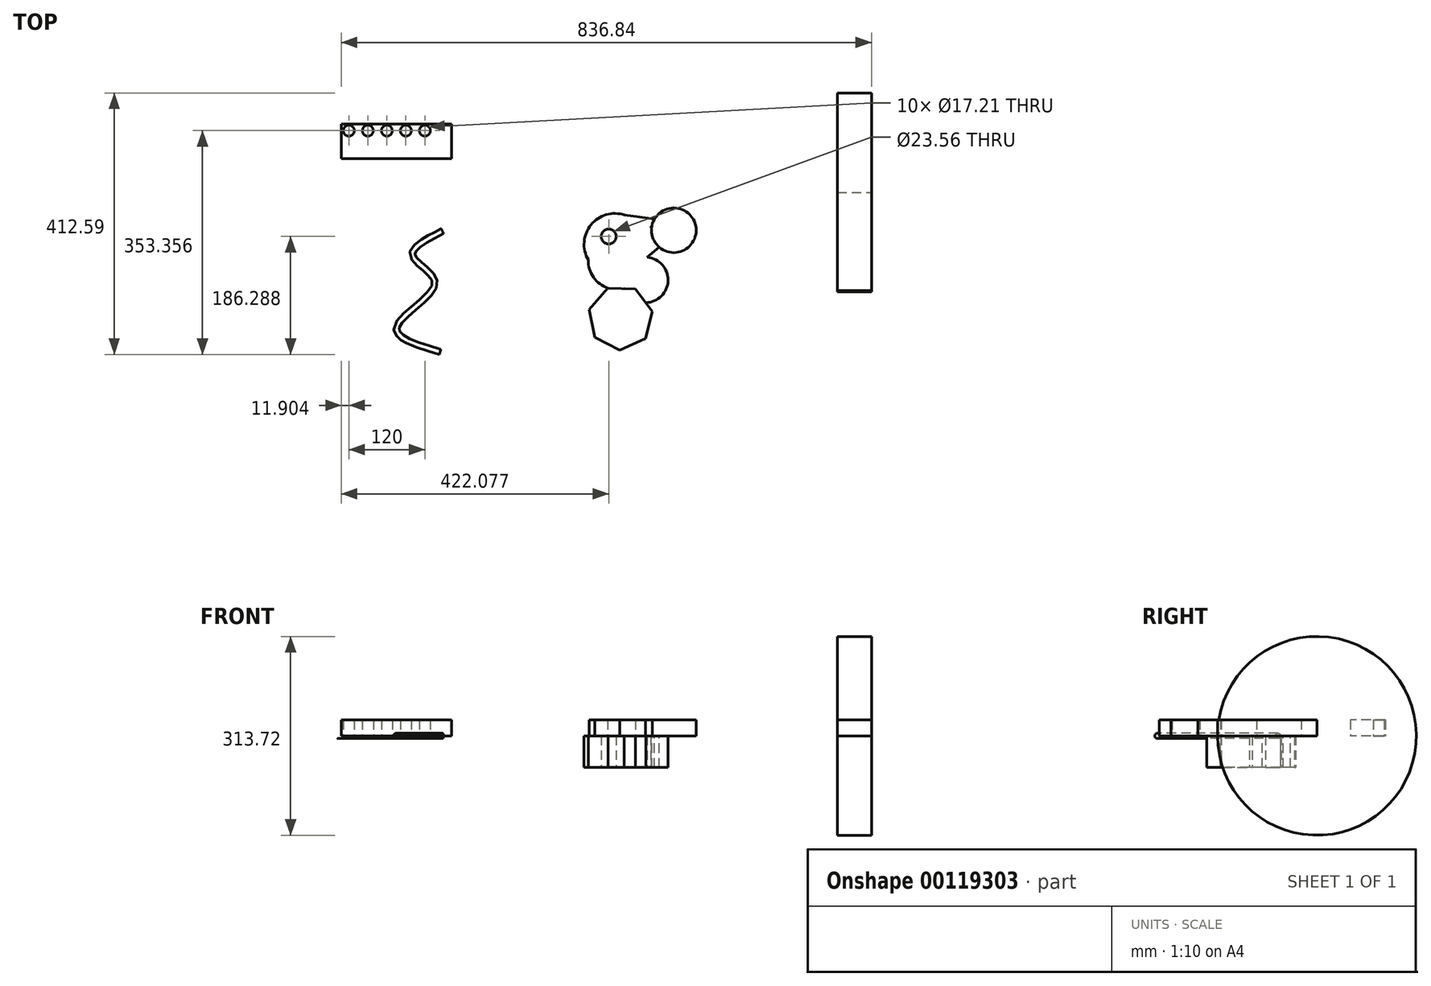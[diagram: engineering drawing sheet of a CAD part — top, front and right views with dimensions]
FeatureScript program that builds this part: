
annotation { "Feature Type Name" : "Feature", "Feature Type Description" : "" }
export const myFeature = defineFeature(function(context is Context, id is Id, definition is map)
    precondition{}
    {
        {
            var Q0;
            Q0=qCreatedBy(makeId("Top.planeOp"),FACE);
            var sketch = newSketch(context, id + "F0", { "sketchPlane" : qUnion([Q0])});
            skLineSegment(sketch, "E0", {"start": v(-37.14, 55.26) * mm, "end": v(11.62, 48.64) * mm});
            skLineSegment(sketch, "E1", {"start": v(11.62, 48.64) * mm, "end": v(4.36, 34.7) * mm});
            skLineSegment(sketch, "E2", {"start": v(4.36, 34.7) * mm, "end": v(23.23, 23.38) * mm});
            skLineSegment(sketch, "E3", {"start": v(23.23, 23.38) * mm, "end": v(40.66, 23.38) * mm});
            skLineSegment(sketch, "E4", {"start": v(40.66, 23.38) * mm, "end": v(-1.5, -11.44) * mm});
            skArc(sketch, "E5", {"start": v(-37.55, -60.76) * mm, "mid": v(24.6, -68.36) * mm, "end": v(-1.5, -11.44) * mm});
            skArc(sketch, "E6", {"start": v(-37.14, 55.26) * mm, "mid": v(-90.15, 39.64) * mm, "end": v(-94.6, -15.44) * mm});
            skArc(sketch, "E7", {"start": v(-94.6, -15.44) * mm, "mid": v(-77.4, -52.36) * mm, "end": v(-37.55, -60.76) * mm});
            skCircle(sketch, "E8", {"center": v(-62.13, 21.43) * mm, "radius": 11.78 * mm});
            skSolve(sketch);
        }
        {
            var Q0;
            Q0=makeQuery(id+"F0.imprint","IMPRINT",FACE,{"disambiguationData":[TD([[makeQuery(id+"F0.imprint","IMPRINT",EDGE,{"derivedFrom":sQuery(id+"F0.wireOp",EDGE,"E0")}),-1.0]])]});
            extrude(context, id + "F1", {"entities" : qUnion([Q0]), "depth" : 50 * mm});
        }
        {
            var Q0;
            Q0=makeQuery(id+"F1.opExtrude","CAP_FACE",FACE,{"disambiguationData":[OSD([sQuery(id+"F0.wireOp",EDGE,"E0"),sQuery(id+"F0.wireOp",EDGE,"E1"),sQuery(id+"F0.wireOp",EDGE,"E2"),sQuery(id+"F0.wireOp",EDGE,"E3"),sQuery(id+"F0.wireOp",EDGE,"E4"),sQuery(id+"F0.wireOp",EDGE,"E5"),sQuery(id+"F0.wireOp",EDGE,"E6"),sQuery(id+"F0.wireOp",EDGE,"E7")])],"isStart":false});
            var sketch = newSketch(context, id + "F2", { "sketchPlane" : qUnion([Q0])});
            skCircle(sketch, "E9.cCircle", {"center": v(-43.3, -106.73) * mm, "radius": 46.05 * mm, "construction": true});
            skLineSegment(sketch, "E9.0", {"start": v(-19.76, -61.36) * mm, "end": v(6.86, -96.85) * mm});
            skLineSegment(sketch, "E9.1", {"start": v(6.86, -96.85) * mm, "end": v(-4.3, -139.78) * mm});
            skLineSegment(sketch, "E9.2", {"start": v(-4.3, -139.78) * mm, "end": v(-44.8, -157.83) * mm});
            skLineSegment(sketch, "E9.3", {"start": v(-44.8, -157.83) * mm, "end": v(-84.18, -137.4) * mm});
            skLineSegment(sketch, "E9.4", {"start": v(-84.18, -137.4) * mm, "end": v(-92.76, -93.89) * mm});
            skLineSegment(sketch, "E9.5", {"start": v(-92.76, -93.89) * mm, "end": v(-64.1, -60.05) * mm});
            skLineSegment(sketch, "E9.6", {"start": v(-64.1, -60.05) * mm, "end": v(-19.76, -61.36) * mm});
            skPoint(sketch, "E9.0.midPoint", {"position": v(-6.45, -79.1) * mm});
            skCircle(sketch, "E10.0", {"center": v(40.57, 31.22) * mm, "radius": 35.26 * mm});
            skLineSegment(sketch, "E11.bottom", {"start": v(298.54, 90.87) * mm, "end": v(352.63, 90.87) * mm});
            skLineSegment(sketch, "E11.top", {"start": v(298.54, -66) * mm, "end": v(352.63, -66) * mm});
            skLineSegment(sketch, "E11.left", {"start": v(298.54, 90.87) * mm, "end": v(298.54, -66) * mm});
            skLineSegment(sketch, "E11.right", {"start": v(352.63, 90.87) * mm, "end": v(352.63, -66) * mm});
            skFitSpline(sketch, "E12", {"points": [v(-324.6, 29.57) * mm, v(-371.49, -9.2) * mm, v(-336.33, -52.47) * mm, v(-396.73, -120.98) * mm, v(-328.22, -160.65) * mm], "startDerivative": vector(-332.37, -164.55) * mm, "endDerivative": vector(418.76, -123.4) * mm});
            skLineSegment(sketch, "E13.bottom", {"start": v(-484.2, 198.96) * mm, "end": v(-310.04, 198.96) * mm});
            skLineSegment(sketch, "E13.top", {"start": v(-484.2, 143.96) * mm, "end": v(-310.04, 143.96) * mm});
            skLineSegment(sketch, "E13.left", {"start": v(-484.2, 198.96) * mm, "end": v(-484.2, 143.96) * mm});
            skLineSegment(sketch, "E13.right", {"start": v(-310.04, 198.96) * mm, "end": v(-310.04, 143.96) * mm});
            skCircle(sketch, "E14", {"center": v(-472.3, 188.5) * mm, "radius": 8.6 * mm});
            skCircle(sketch, "E15.1.0.0", {"center": v(-442.3, 188.5) * mm, "radius": 8.6 * mm});
            skCircle(sketch, "E15.2.0.0", {"center": v(-412.3, 188.5) * mm, "radius": 8.6 * mm});
            skCircle(sketch, "E15.3.0.0", {"center": v(-382.3, 188.5) * mm, "radius": 8.6 * mm});
            skCircle(sketch, "E15.4.0.0", {"center": v(-352.3, 188.5) * mm, "radius": 8.6 * mm});
            skLineSegment(sketch, "E15.direction1", {"start": v(-472.3, 188.5) * mm, "end": v(-442.3, 188.5) * mm, "construction": true});
            skSolve(sketch);
        }
        {
            var Q0;
            Q0 = qSketchRegion(id + "F2", true);
            extrude(context, id + "F3", {"entities" : qUnion([Q0]), "operationType" : NewBodyOperationType.REMOVE, "oppositeDirection" : true, "depth" : 50 * mm});
        }
        {
            var Q0;
            Q0=makeQuery(id+"F2.imprint","IMPRINT",FACE,{"disambiguationData":[TD([[makeQuery(id+"F2.imprint","IMPRINT",EDGE,{"derivedFrom":sQuery(id+"F2.wireOp",EDGE,"E11.bottom")}),-1.0]])]});
            var Q1;
            Q1=sQuery(id+"F2.wireOp",EDGE,"E11.bottom");
            revolve(context, id + "F4", {"entities" : qUnion([Q0]), "axis" : qUnion([Q1]), "revolveType" : RevolveType.FULL, "oppositeDirection" : true});
        }
        {
            var Q0;
            Q0 = qSketchRegion(id + "F2", true);
            extrude(context, id + "F5", {"entities" : qUnion([Q0]), "operationType" : NewBodyOperationType.ADD, "depth" : 25 * mm});
        }
        {
            var Q0;
            Q0 = qSketchRegion(id + "F2", true);
            var Q1;
            Q1=makeQuery(id+"F2.imprint","IMPRINT",FACE,{"disambiguationData":[TD([[makeQuery(id+"F2.imprint","IMPRINT",EDGE,{"derivedFrom":sQuery(id+"F2.wireOp",EDGE,"E13.bottom")}),-1.0]])]});
            extrude(context, id + "F6", {"entities" : qUnion([Q0, Q1]), "depth" : 25 * mm});
        }
        {
            var Q0;
            Q0=sQuery(id+"F2.wireOp",EDGE,"E12");
            var Q1;
            Q1=sQuery(id+"F2.wireOp",VERTEX,"E12.4.internal");
            cPlane(context, id + "F7", {"entities" : qUnion([Q0, Q1]), "cplaneType" : CPlaneType.CURVE_POINT, "offset" : 25 * mm, "width" : 150 * mm, "height" : 150 * mm});
        }
        {
            var Q0;
            Q0=qCreatedBy(id+"F7.planeOp",FACE);
            var sketch = newSketch(context, id + "F8", { "sketchPlane" : qUnion([Q0])});
            skCircle(sketch, "E16", {"center": v(-247.01, 49.93) * mm, "radius": 4.24 * mm});
            skSolve(sketch);
        }
        {
            var Q0;
            Q0=makeQuery(id+"F8.imprint","IMPRINT",FACE,{"disambiguationData":[TD([[makeQuery(id+"F8.imprint","IMPRINT",EDGE,{"derivedFrom":sQuery(id+"F8.wireOp",EDGE,"E16")}),1.0]])]});
            var Q1;
            Q1=sQuery(id+"F2.wireOp",EDGE,"E12");
            sweep(context, id + "F9", {"profiles" : qUnion([Q0]), "path" : qUnion([Q1])});
        }
    });
